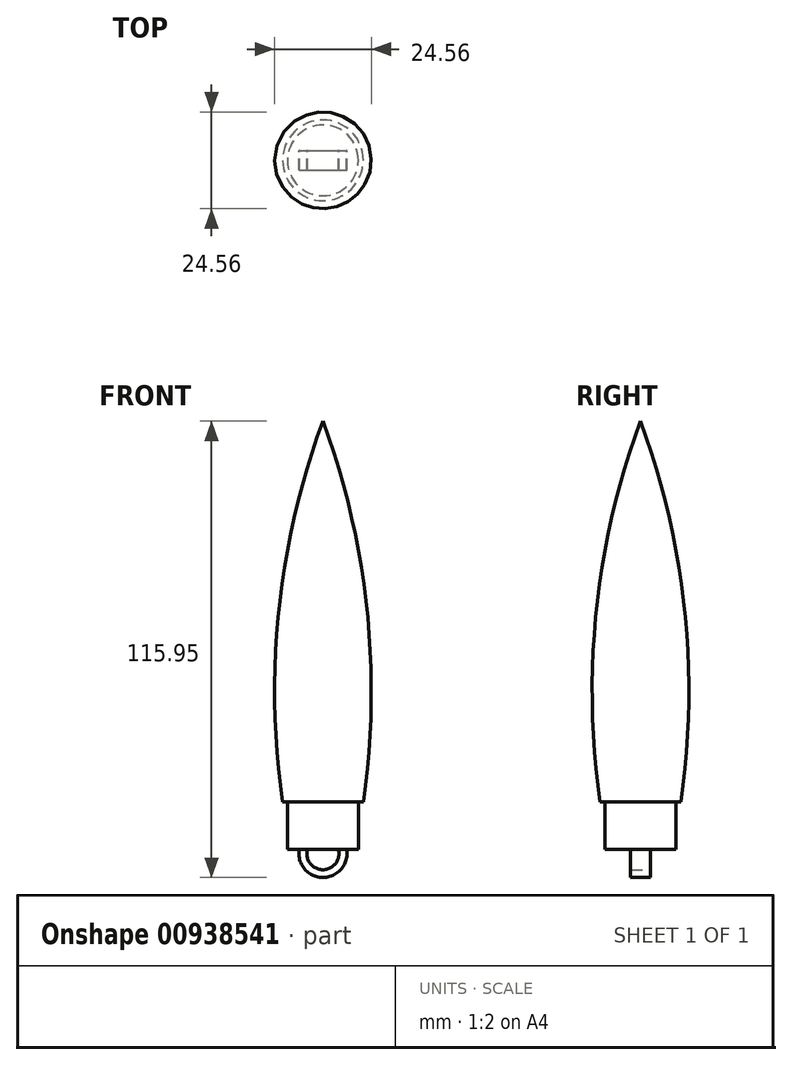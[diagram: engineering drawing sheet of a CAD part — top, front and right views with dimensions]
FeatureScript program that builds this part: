
annotation { "Feature Type Name" : "Feature", "Feature Type Description" : "" }
export const myFeature = defineFeature(function(context is Context, id is Id, definition is map)
    precondition{}
    {
        {
            var Q0;
            Q0=qCreatedBy(makeId("Front.planeOp"),FACE);
            var sketch = newSketch(context, id + "F0", { "sketchPlane" : qUnion([Q0])});
            skLineSegment(sketch, "E0", {"start": v(0, 108.75) * mm, "end": v(0, 0) * mm});
            skLineSegment(sketch, "E1", {"start": v(0, 0) * mm, "end": v(9, 0) * mm});
            skLineSegment(sketch, "E2", {"start": v(9, 0) * mm, "end": v(9, 12) * mm});
            skLineSegment(sketch, "E3", {"start": v(9, 12) * mm, "end": v(10.25, 12) * mm});
            skArc(sketch, "E4", {"start": v(10.25, 12) * mm, "mid": v(11.18, 61.02) * mm, "end": v(0, 108.75) * mm});
            skSolve(sketch);
        }
        {
            var Q0;
            Q0=makeQuery(id+"F0.imprint","IMPRINT",FACE,{"disambiguationData":[TD([[makeQuery(id+"F0.imprint","IMPRINT",EDGE,{"derivedFrom":sQuery(id+"F0.wireOp",EDGE,"E0")}),1.0]])]});
            var Q1;
            Q1=sQuery(id+"F0.wireOp",EDGE,"E0");
            revolve(context, id + "F1", {"surfaceOperationType" : NewSurfaceOperationType.NEW, "entities" : qUnion([Q0]), "axis" : qUnion([Q1]), "revolveType" : RevolveType.FULL});
        }
        {
            var Q0;
            Q0=qCreatedBy(makeId("Front.planeOp"),FACE);
            var sketch = newSketch(context, id + "F2", { "sketchPlane" : qUnion([Q0])});
            skArc(sketch, "E5", {"start": v(-6, 0) * mm, "mid": v(0, -7.2) * mm, "end": v(6, 0) * mm});
            skArc(sketch, "E6.0", {"start": v(-3.95, 0) * mm, "mid": v(0, -5.2) * mm, "end": v(3.95, 0) * mm});
            skLineSegment(sketch, "E7", {"start": v(-6, 0) * mm, "end": v(6, 0) * mm});
            skSolve(sketch);
        }
        {
            var Q0;
            {var subQ0=sQuery(id+"F2.wireOp",EDGE,"E5");Q0=makeQuery(id+"F2.imprint","IMPRINT",FACE,{"disambiguationData":[TD([[makeQuery(id+"F2.imprint","IMPRINT",EDGE,{"derivedFrom":subQ0}),1.0]])]});}
            extrude(context, id + "F3", {"entities" : qUnion([Q0]), "operationType" : NewBodyOperationType.ADD, "endBound" : BoundingType.SYMMETRIC, "depth" : 5 * mm, "offsetDistance" : 25 * mm});
        }
    });
